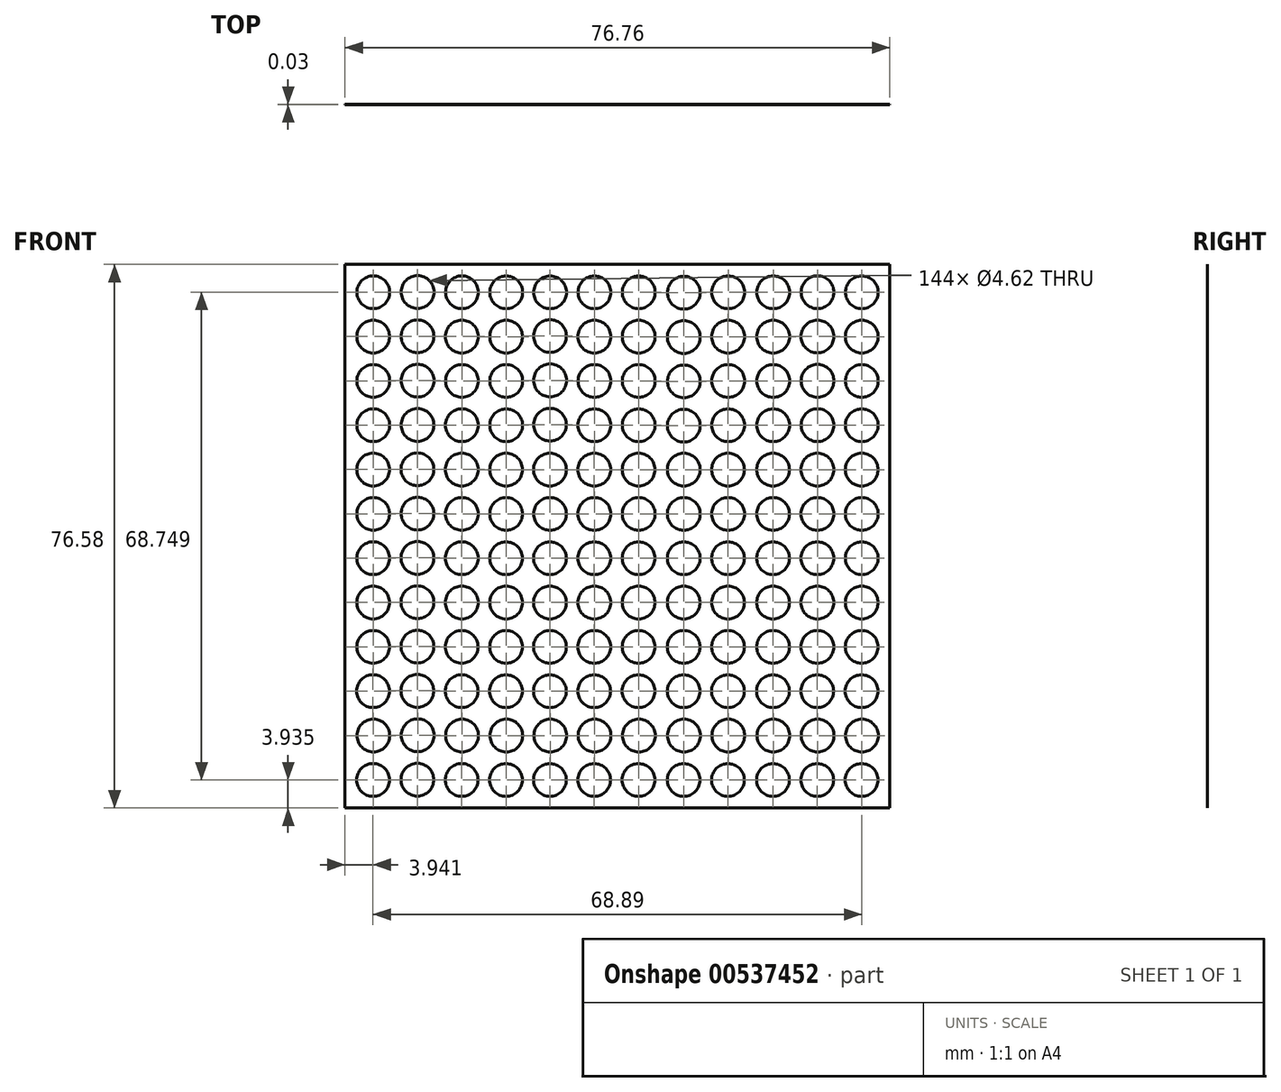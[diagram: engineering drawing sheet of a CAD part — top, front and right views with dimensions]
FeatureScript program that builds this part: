
annotation { "Feature Type Name" : "Feature", "Feature Type Description" : "" }
export const myFeature = defineFeature(function(context is Context, id is Id, definition is map)
    precondition{}
    {
        {
            var Q0;
            Q0=qCreatedBy(makeId("Front.planeOp"),FACE);
            var sketch = newSketch(context, id + "F0", { "sketchPlane" : qUnion([Q0])});
            skLineSegment(sketch, "E0", {"start": v(0, 0) * mm, "end": v(76.76, 0) * mm});
            skLineSegment(sketch, "E1", {"start": v(76.76, 0) * mm, "end": v(76.76, 76.58) * mm});
            skLineSegment(sketch, "E2", {"start": v(76.76, 76.58) * mm, "end": v(0, 76.58) * mm});
            skLineSegment(sketch, "E3", {"start": v(0, 76.58) * mm, "end": v(0, 0) * mm});
            skPoint(sketch, "E4", {"position": v(0, 38.29) * mm});
            skPoint(sketch, "E5", {"position": v(38.38, 0) * mm});
            skLineSegment(sketch, "E6", {"start": v(57.57, 76.58) * mm, "end": v(19.2, 76.58) * mm});
            skLineSegment(sketch, "E7", {"start": v(19.2, 0) * mm, "end": v(57.57, 0) * mm});
            skCircle(sketch, "E8", {"center": v(3.94, 3.94) * mm, "radius": 2.3 * mm});
            skCircle(sketch, "E9", {"center": v(4, 10.2) * mm, "radius": 2.3 * mm});
            skCircle(sketch, "E10", {"center": v(3.94, 16.45) * mm, "radius": 2.3 * mm});
            skCircle(sketch, "E11", {"center": v(3.95, 22.7) * mm, "radius": 2.3 * mm});
            skCircle(sketch, "E12", {"center": v(3.96, 28.94) * mm, "radius": 2.3 * mm});
            skCircle(sketch, "E13", {"center": v(3.95, 35.19) * mm, "radius": 2.3 * mm});
            skCircle(sketch, "E14", {"center": v(3.96, 41.43) * mm, "radius": 2.3 * mm});
            skCircle(sketch, "E15", {"center": v(3.95, 47.67) * mm, "radius": 2.3 * mm});
            skCircle(sketch, "E16", {"center": v(3.97, 53.92) * mm, "radius": 2.3 * mm});
            skCircle(sketch, "E17", {"center": v(3.98, 60.16) * mm, "radius": 2.3 * mm});
            skCircle(sketch, "E18", {"center": v(3.97, 66.4) * mm, "radius": 2.3 * mm});
            skCircle(sketch, "E19", {"center": v(3.98, 72.65) * mm, "radius": 2.3 * mm});
            skCircle(sketch, "E20", {"center": v(10.19, 3.98) * mm, "radius": 2.3 * mm});
            skCircle(sketch, "E21", {"center": v(10.23, 10.23) * mm, "radius": 2.3 * mm});
            skCircle(sketch, "E22", {"center": v(10.18, 16.49) * mm, "radius": 2.3 * mm});
            skCircle(sketch, "E23", {"center": v(10.2, 22.73) * mm, "radius": 2.3 * mm});
            skCircle(sketch, "E24", {"center": v(10.2, 28.98) * mm, "radius": 2.3 * mm});
            skCircle(sketch, "E25", {"center": v(10.2, 35.22) * mm, "radius": 2.3 * mm});
            skCircle(sketch, "E26", {"center": v(10.2, 41.46) * mm, "radius": 2.3 * mm});
            skCircle(sketch, "E27", {"center": v(10.2, 47.7) * mm, "radius": 2.3 * mm});
            skCircle(sketch, "E28", {"center": v(10.21, 53.95) * mm, "radius": 2.3 * mm});
            skCircle(sketch, "E29", {"center": v(10.22, 60.2) * mm, "radius": 2.3 * mm});
            skCircle(sketch, "E30", {"center": v(10.2, 66.44) * mm, "radius": 2.3 * mm});
            skCircle(sketch, "E31", {"center": v(10.22, 72.68) * mm, "radius": 2.3 * mm});
            skCircle(sketch, "E32", {"center": v(16.43, 3.94) * mm, "radius": 2.3 * mm});
            skCircle(sketch, "E33", {"center": v(16.48, 10.2) * mm, "radius": 2.3 * mm});
            skCircle(sketch, "E34", {"center": v(16.43, 16.45) * mm, "radius": 2.3 * mm});
            skCircle(sketch, "E35", {"center": v(16.44, 22.7) * mm, "radius": 2.3 * mm});
            skCircle(sketch, "E36", {"center": v(16.45, 28.94) * mm, "radius": 2.3 * mm});
            skCircle(sketch, "E37", {"center": v(16.44, 35.18) * mm, "radius": 2.3 * mm});
            skCircle(sketch, "E38", {"center": v(16.45, 41.43) * mm, "radius": 2.3 * mm});
            skCircle(sketch, "E39", {"center": v(16.44, 47.67) * mm, "radius": 2.3 * mm});
            skCircle(sketch, "E40", {"center": v(16.45, 53.91) * mm, "radius": 2.3 * mm});
            skCircle(sketch, "E41", {"center": v(16.46, 60.16) * mm, "radius": 2.3 * mm});
            skCircle(sketch, "E42", {"center": v(16.45, 66.4) * mm, "radius": 2.3 * mm});
            skCircle(sketch, "E43", {"center": v(16.46, 72.65) * mm, "radius": 2.3 * mm});
            skCircle(sketch, "E44", {"center": v(22.67, 3.93) * mm, "radius": 2.3 * mm});
            skCircle(sketch, "E45", {"center": v(22.72, 10.2) * mm, "radius": 2.3 * mm});
            skCircle(sketch, "E46", {"center": v(22.67, 16.45) * mm, "radius": 2.3 * mm});
            skCircle(sketch, "E47", {"center": v(22.69, 22.7) * mm, "radius": 2.3 * mm});
            skCircle(sketch, "E48", {"center": v(22.69, 28.93) * mm, "radius": 2.3 * mm});
            skCircle(sketch, "E49", {"center": v(22.69, 35.18) * mm, "radius": 2.3 * mm});
            skCircle(sketch, "E50", {"center": v(22.7, 41.42) * mm, "radius": 2.3 * mm});
            skCircle(sketch, "E51", {"center": v(22.69, 47.67) * mm, "radius": 2.3 * mm});
            skCircle(sketch, "E52", {"center": v(22.7, 53.9) * mm, "radius": 2.3 * mm});
            skCircle(sketch, "E53", {"center": v(22.7, 60.15) * mm, "radius": 2.3 * mm});
            skCircle(sketch, "E54", {"center": v(22.7, 66.4) * mm, "radius": 2.3 * mm});
            skCircle(sketch, "E55", {"center": v(22.7, 72.64) * mm, "radius": 2.3 * mm});
            skCircle(sketch, "E56", {"center": v(28.86, 3.93) * mm, "radius": 2.3 * mm});
            skCircle(sketch, "E57", {"center": v(28.9, 10.2) * mm, "radius": 2.3 * mm});
            skCircle(sketch, "E58", {"center": v(28.86, 16.45) * mm, "radius": 2.3 * mm});
            skCircle(sketch, "E59", {"center": v(28.87, 22.7) * mm, "radius": 2.3 * mm});
            skCircle(sketch, "E60", {"center": v(28.87, 28.93) * mm, "radius": 2.3 * mm});
            skCircle(sketch, "E61", {"center": v(28.87, 35.18) * mm, "radius": 2.3 * mm});
            skCircle(sketch, "E62", {"center": v(28.88, 41.42) * mm, "radius": 2.3 * mm});
            skCircle(sketch, "E63", {"center": v(28.87, 47.67) * mm, "radius": 2.3 * mm});
            skCircle(sketch, "E64", {"center": v(28.89, 54) * mm, "radius": 2.3 * mm});
            skCircle(sketch, "E65", {"center": v(28.9, 60.24) * mm, "radius": 2.3 * mm});
            skCircle(sketch, "E66", {"center": v(28.88, 66.48) * mm, "radius": 2.3 * mm});
            skCircle(sketch, "E67", {"center": v(28.9, 72.63) * mm, "radius": 2.3 * mm});
            skCircle(sketch, "E68", {"center": v(35.1, 3.93) * mm, "radius": 2.3 * mm});
            skCircle(sketch, "E69", {"center": v(35.15, 10.2) * mm, "radius": 2.3 * mm});
            skCircle(sketch, "E70", {"center": v(35.1, 16.45) * mm, "radius": 2.3 * mm});
            skCircle(sketch, "E71", {"center": v(35.11, 22.7) * mm, "radius": 2.3 * mm});
            skCircle(sketch, "E72", {"center": v(35.12, 28.93) * mm, "radius": 2.3 * mm});
            skCircle(sketch, "E73", {"center": v(35.12, 35.18) * mm, "radius": 2.3 * mm});
            skCircle(sketch, "E74", {"center": v(35.13, 41.42) * mm, "radius": 2.3 * mm});
            skCircle(sketch, "E75", {"center": v(35.12, 47.67) * mm, "radius": 2.3 * mm});
            skCircle(sketch, "E76", {"center": v(35.13, 53.9) * mm, "radius": 2.3 * mm});
            skCircle(sketch, "E77", {"center": v(35.14, 60.15) * mm, "radius": 2.3 * mm});
            skCircle(sketch, "E78", {"center": v(35.13, 66.4) * mm, "radius": 2.3 * mm});
            skCircle(sketch, "E79", {"center": v(35.14, 72.64) * mm, "radius": 2.3 * mm});
            skCircle(sketch, "E80", {"center": v(41.35, 3.93) * mm, "radius": 2.3 * mm});
            skCircle(sketch, "E81", {"center": v(41.4, 10.2) * mm, "radius": 2.3 * mm});
            skCircle(sketch, "E82", {"center": v(41.35, 16.45) * mm, "radius": 2.3 * mm});
            skCircle(sketch, "E83", {"center": v(41.35, 22.7) * mm, "radius": 2.3 * mm});
            skCircle(sketch, "E84", {"center": v(41.36, 28.93) * mm, "radius": 2.3 * mm});
            skCircle(sketch, "E85", {"center": v(41.36, 35.18) * mm, "radius": 2.3 * mm});
            skCircle(sketch, "E86", {"center": v(41.37, 41.42) * mm, "radius": 2.3 * mm});
            skCircle(sketch, "E87", {"center": v(41.36, 47.67) * mm, "radius": 2.3 * mm});
            skCircle(sketch, "E88", {"center": v(41.37, 53.9) * mm, "radius": 2.3 * mm});
            skCircle(sketch, "E89", {"center": v(41.38, 60.15) * mm, "radius": 2.3 * mm});
            skCircle(sketch, "E90", {"center": v(41.37, 66.4) * mm, "radius": 2.3 * mm});
            skCircle(sketch, "E91", {"center": v(41.38, 72.64) * mm, "radius": 2.3 * mm});
            skCircle(sketch, "E92", {"center": v(47.7, 3.93) * mm, "radius": 2.3 * mm});
            skCircle(sketch, "E93", {"center": v(47.75, 10.2) * mm, "radius": 2.3 * mm});
            skCircle(sketch, "E94", {"center": v(47.7, 16.45) * mm, "radius": 2.3 * mm});
            skCircle(sketch, "E95", {"center": v(47.71, 22.7) * mm, "radius": 2.3 * mm});
            skCircle(sketch, "E96", {"center": v(47.72, 28.93) * mm, "radius": 2.3 * mm});
            skCircle(sketch, "E97", {"center": v(47.72, 35.18) * mm, "radius": 2.3 * mm});
            skCircle(sketch, "E98", {"center": v(47.73, 41.42) * mm, "radius": 2.3 * mm});
            skCircle(sketch, "E99", {"center": v(47.72, 47.67) * mm, "radius": 2.3 * mm});
            skCircle(sketch, "E100", {"center": v(47.73, 53.85) * mm, "radius": 2.3 * mm});
            skCircle(sketch, "E101", {"center": v(47.74, 60.1) * mm, "radius": 2.3 * mm});
            skCircle(sketch, "E102", {"center": v(47.73, 66.34) * mm, "radius": 2.3 * mm});
            skCircle(sketch, "E103", {"center": v(47.74, 72.58) * mm, "radius": 2.3 * mm});
            skCircle(sketch, "E104", {"center": v(53.95, 3.93) * mm, "radius": 2.3 * mm});
            skCircle(sketch, "E105", {"center": v(54, 10.2) * mm, "radius": 2.3 * mm});
            skCircle(sketch, "E106", {"center": v(53.95, 16.45) * mm, "radius": 2.3 * mm});
            skCircle(sketch, "E107", {"center": v(53.96, 22.7) * mm, "radius": 2.3 * mm});
            skCircle(sketch, "E108", {"center": v(53.96, 28.93) * mm, "radius": 2.3 * mm});
            skCircle(sketch, "E109", {"center": v(53.96, 35.18) * mm, "radius": 2.3 * mm});
            skCircle(sketch, "E110", {"center": v(53.97, 41.42) * mm, "radius": 2.3 * mm});
            skCircle(sketch, "E111", {"center": v(53.96, 47.67) * mm, "radius": 2.3 * mm});
            skCircle(sketch, "E112", {"center": v(53.97, 53.9) * mm, "radius": 2.3 * mm});
            skCircle(sketch, "E113", {"center": v(53.98, 60.15) * mm, "radius": 2.3 * mm});
            skCircle(sketch, "E114", {"center": v(53.97, 66.4) * mm, "radius": 2.3 * mm});
            skCircle(sketch, "E115", {"center": v(53.98, 72.64) * mm, "radius": 2.3 * mm});
            skCircle(sketch, "E116", {"center": v(60.3, 3.93) * mm, "radius": 2.3 * mm});
            skCircle(sketch, "E117", {"center": v(60.34, 10.2) * mm, "radius": 2.3 * mm});
            skCircle(sketch, "E118", {"center": v(60.3, 16.45) * mm, "radius": 2.3 * mm});
            skCircle(sketch, "E119", {"center": v(60.3, 22.7) * mm, "radius": 2.3 * mm});
            skCircle(sketch, "E120", {"center": v(60.3, 28.93) * mm, "radius": 2.3 * mm});
            skCircle(sketch, "E121", {"center": v(60.3, 35.18) * mm, "radius": 2.3 * mm});
            skCircle(sketch, "E122", {"center": v(60.32, 41.42) * mm, "radius": 2.3 * mm});
            skCircle(sketch, "E123", {"center": v(60.3, 47.67) * mm, "radius": 2.3 * mm});
            skCircle(sketch, "E124", {"center": v(60.32, 53.9) * mm, "radius": 2.3 * mm});
            skCircle(sketch, "E125", {"center": v(60.33, 60.15) * mm, "radius": 2.3 * mm});
            skCircle(sketch, "E126", {"center": v(60.32, 66.4) * mm, "radius": 2.3 * mm});
            skCircle(sketch, "E127", {"center": v(60.33, 72.64) * mm, "radius": 2.3 * mm});
            skCircle(sketch, "E128", {"center": v(66.54, 3.93) * mm, "radius": 2.3 * mm});
            skCircle(sketch, "E129", {"center": v(66.59, 10.2) * mm, "radius": 2.3 * mm});
            skCircle(sketch, "E130", {"center": v(66.54, 16.45) * mm, "radius": 2.3 * mm});
            skCircle(sketch, "E131", {"center": v(66.55, 22.7) * mm, "radius": 2.3 * mm});
            skCircle(sketch, "E132", {"center": v(66.55, 28.93) * mm, "radius": 2.3 * mm});
            skCircle(sketch, "E133", {"center": v(66.55, 35.18) * mm, "radius": 2.3 * mm});
            skCircle(sketch, "E134", {"center": v(66.56, 41.42) * mm, "radius": 2.3 * mm});
            skCircle(sketch, "E135", {"center": v(66.55, 47.67) * mm, "radius": 2.3 * mm});
            skCircle(sketch, "E136", {"center": v(66.56, 53.92) * mm, "radius": 2.3 * mm});
            skCircle(sketch, "E137", {"center": v(66.57, 60.17) * mm, "radius": 2.3 * mm});
            skCircle(sketch, "E138", {"center": v(66.56, 66.41) * mm, "radius": 2.3 * mm});
            skCircle(sketch, "E139", {"center": v(66.57, 72.66) * mm, "radius": 2.3 * mm});
            skCircle(sketch, "E140", {"center": v(72.78, 3.93) * mm, "radius": 2.3 * mm});
            skCircle(sketch, "E141", {"center": v(72.83, 10.2) * mm, "radius": 2.3 * mm});
            skCircle(sketch, "E142", {"center": v(72.78, 16.45) * mm, "radius": 2.3 * mm});
            skCircle(sketch, "E143", {"center": v(72.8, 22.7) * mm, "radius": 2.3 * mm});
            skCircle(sketch, "E144", {"center": v(72.8, 28.93) * mm, "radius": 2.3 * mm});
            skCircle(sketch, "E145", {"center": v(72.8, 35.18) * mm, "radius": 2.3 * mm});
            skCircle(sketch, "E146", {"center": v(72.8, 41.42) * mm, "radius": 2.3 * mm});
            skCircle(sketch, "E147", {"center": v(72.8, 47.67) * mm, "radius": 2.3 * mm});
            skCircle(sketch, "E148", {"center": v(72.8, 53.9) * mm, "radius": 2.3 * mm});
            skCircle(sketch, "E149", {"center": v(72.82, 60.15) * mm, "radius": 2.3 * mm});
            skCircle(sketch, "E150", {"center": v(72.8, 66.4) * mm, "radius": 2.3 * mm});
            skCircle(sketch, "E151", {"center": v(72.82, 72.64) * mm, "radius": 2.3 * mm});
            skSolve(sketch);
        }
        {
            var Q0;
            {var subQ1=sQuery(id+"F0.wireOp",EDGE,"E1");Q0=makeQuery(id+"F0.imprint","IMPRINT",FACE,{"disambiguationData":[TD([[makeQuery(id+"F0.imprint","IMPRINT",EDGE,{"derivedFrom":subQ1}),1.0]])]});}
            extrude(context, id + "F1", {"entities" : qUnion([Q0]), "depth" : 0.03 * mm, "offsetDistance" : 25.4 * mm});
        }
    });
